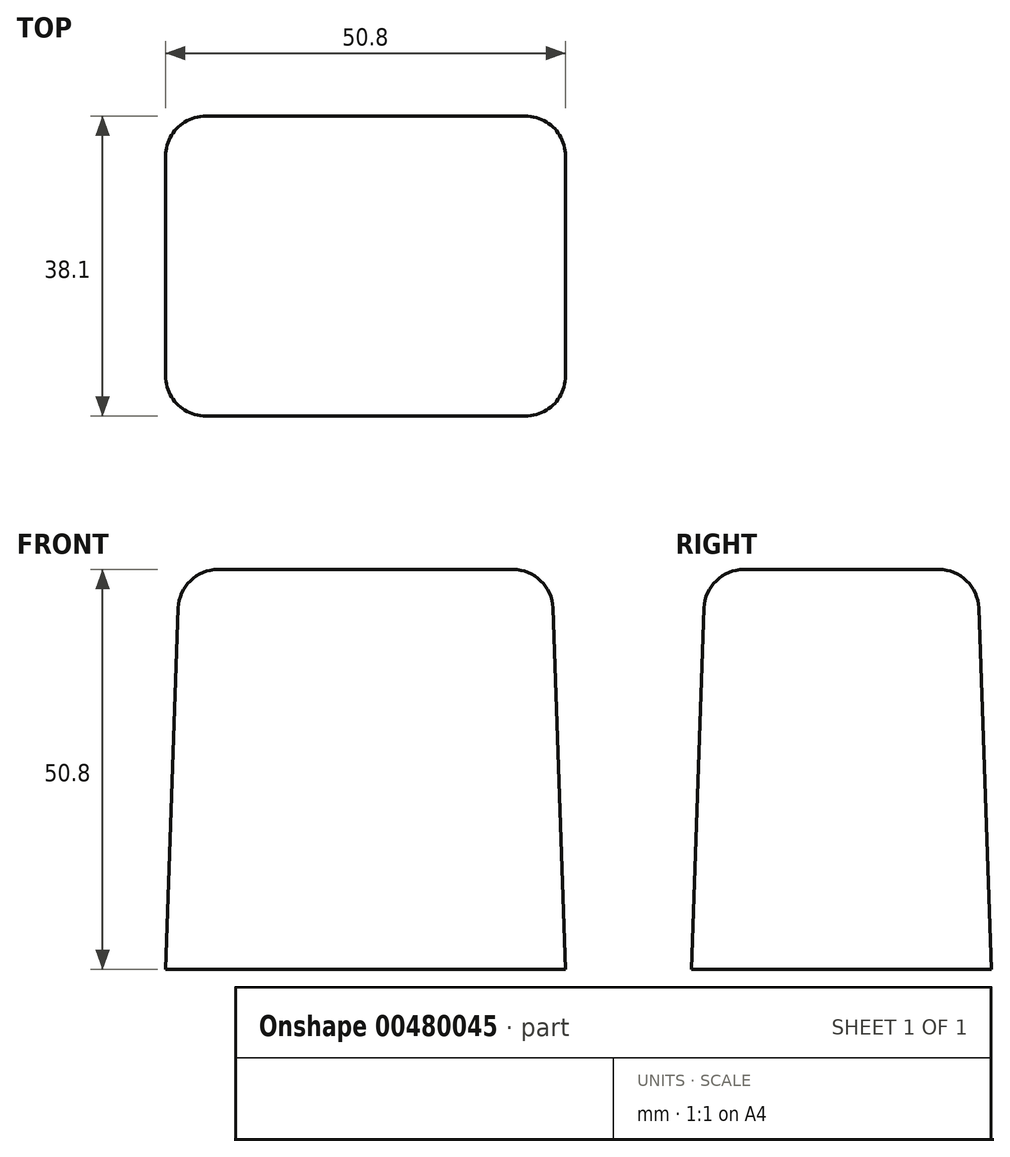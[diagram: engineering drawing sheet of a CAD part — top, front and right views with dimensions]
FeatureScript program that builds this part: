
annotation { "Feature Type Name" : "Feature", "Feature Type Description" : "" }
export const myFeature = defineFeature(function(context is Context, id is Id, definition is map)
    precondition{}
    {
        {
            var Q0;
            Q0=qCreatedBy(makeId("Top.planeOp"),FACE);
            var sketch = newSketch(context, id + "F0", { "sketchPlane" : qUnion([Q0])});
            skLineSegment(sketch, "E0.bottom", {"start": v(0, 0) * mm, "end": v(50.8, 0) * mm});
            skLineSegment(sketch, "E0.top", {"start": v(0, 38.1) * mm, "end": v(50.8, 38.1) * mm});
            skLineSegment(sketch, "E0.left", {"start": v(0, 0) * mm, "end": v(0, 38.1) * mm});
            skLineSegment(sketch, "E0.right", {"start": v(50.8, 0) * mm, "end": v(50.8, 38.1) * mm});
            skSolve(sketch);
        }
        {
            var Q0;
            Q0=makeQuery(id+"F0.imprint","IMPRINT",FACE,{"disambiguationData":[TD([[makeQuery(id+"F0.imprint","IMPRINT",EDGE,{"derivedFrom":sQuery(id+"F0.wireOp",EDGE,"E0.bottom")}),1.0]])]});
            extrude(context, id + "F1", {"entities" : qUnion([Q0]), "depth" : 50.8 * mm, "hasDraft" : true, "draftAngle" : 2 * degree, "draftPullDirection" : true});
        }
        {
            var Q0;
            Q0=makeQuery(id+"F1.opExtrude","SWEPT_EDGE",EDGE,{"disambiguationData":[OSD([sQuery(id+"F0.wireOp",EDGE,"E0.top"),sQuery(id+"F0.wireOp",EDGE,"E0.right")])]});
            var Q1;
            Q1=makeQuery(id+"F1.opExtrude","SWEPT_EDGE",EDGE,{"disambiguationData":[OSD([sQuery(id+"F0.wireOp",EDGE,"E0.bottom"),sQuery(id+"F0.wireOp",EDGE,"E0.right")])]});
            var Q2;
            Q2=makeQuery(id+"F1.opExtrude","SWEPT_EDGE",EDGE,{"disambiguationData":[OSD([sQuery(id+"F0.wireOp",EDGE,"E0.bottom"),sQuery(id+"F0.wireOp",EDGE,"E0.left")])]});
            var Q3;
            Q3=makeQuery(id+"F1.opExtrude","SWEPT_EDGE",EDGE,{"disambiguationData":[OSD([sQuery(id+"F0.wireOp",EDGE,"E0.top"),sQuery(id+"F0.wireOp",EDGE,"E0.left")])]});
            fillet(context, id + "F2", {"entities" : qUnion([Q0, Q1, Q2, Q3]), "radius" : 5.08 * mm, "tangentPropagation" : true, "allowEdgeOverflow" : false});
        }
        {
            var Q0;
            Q0=makeQuery(id+"F1.opExtrude","CAP_EDGE",EDGE,{"disambiguationData":[OSD([sQuery(id+"F0.wireOp",EDGE,"E0.bottom")])],"isStart":false});
            fillet(context, id + "F3", {"entities" : qUnion([Q0]), "radius" : 5.08 * mm, "tangentPropagation" : true, "allowEdgeOverflow" : false});
        }
    });
